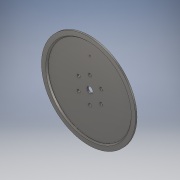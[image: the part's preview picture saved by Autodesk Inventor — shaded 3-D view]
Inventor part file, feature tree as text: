
AUTODESK INVENTOR PART (.ipt)
format: ipt  version: 2019.4 (Build 234330000, 330)  size: 153,088 bytes
history: native  units: mm
features: extrude x4, sketch x3, chamfer x2, plane x1
ambient origin geometry x8: Origin, YZ Plane, XZ Plane, XY Plane, X Axis, Y Axis, Z Axis, Center Point
bodies: Solid1 (feature_tree)
feature tree (10):
  sketch  "Sketch1"  dims[d0=310.0mm d1=20.0mm]
  extrude  "Extrusion1"  Depth=20.0mm
  extrude  "Extrusion2"  Depth=5.0mm TaperAngle=0.0deg
  chamfer  "Chamfer1"  Distance=5.0mm
  chamfer  "Chamfer2"  Distance=4.0mm Angle=45.0deg
  plane  "Work Plane1"
  extrude  "Extrusion4"  Depth=5.0mm TaperAngle=45.0deg
  sketch  "Sketch3"  dims[d8=60.0mm d9=360.0deg d10=10.0mm d11=43.0mm d13=0.0mm d14=5.0mm d15=4.0mm d16=2.0mm d17=45.0deg d18=4.0mm d19=2.0mm d20=45.0deg d21=0.0mm d23=5.0mm d24=5.0mm d25=0.0mm d26=40.0mm]
  sketch  "Sketch2"  dims[d2=274.0mm d3=5.0mm d4=0.0mm d5=5.0mm d6=0.0mm]
  extrude  "Extrusion3"  TaperAngle=0.0deg  [1 undecoded]
note: 1 required parameter value undecoded (feature->parameter linkage not recoverable at this tier; creation-order binding heuristic only, values carry confidence <= 0.55)
